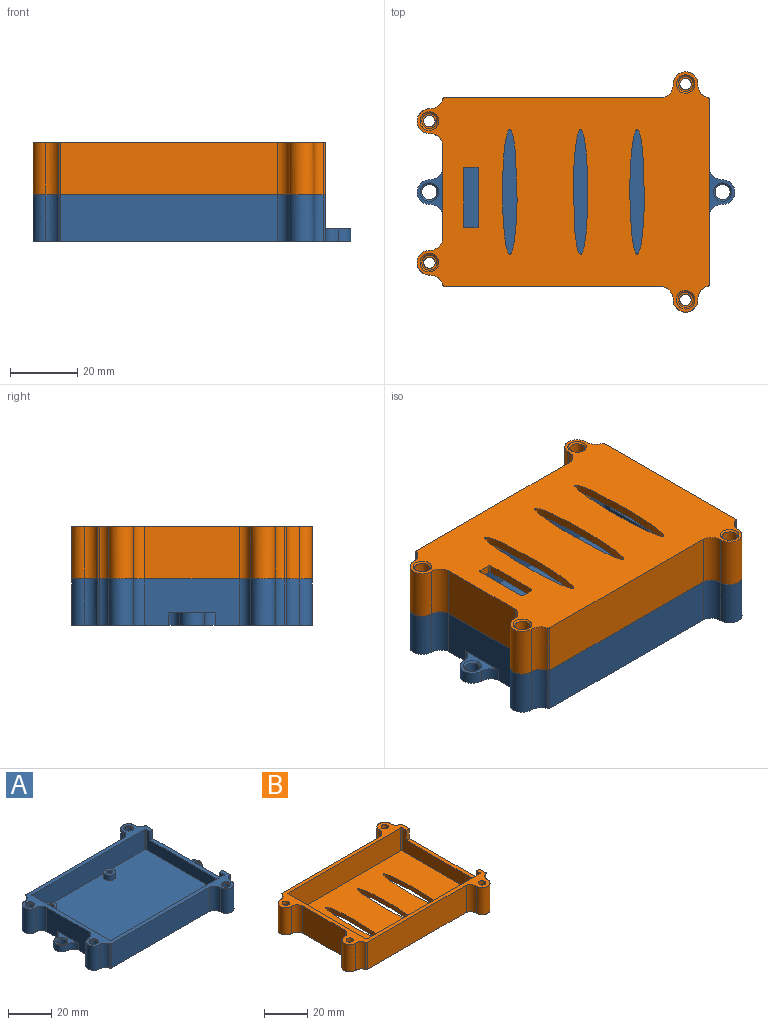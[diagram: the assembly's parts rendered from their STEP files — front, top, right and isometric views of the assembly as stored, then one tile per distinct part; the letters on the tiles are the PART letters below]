
ASSEMBLY  parts=2 mates=1
PART A: 82 faces, bbox 94.3x71.3x13.8 mm
  f0: plane 28x13.8mm, normal (-1,0,0), area 334.6mm2, adj f10,f11,f38,f40,f50,f69,f71
  f1: plane 64.5x13.8mm, normal (0,-1,0), area 890.1mm2, adj f14,f15,f50,f71
  f2: plane 55x13.8mm, normal (1,0,0), area 481.8mm2, adj f18,f19,f28,f29,f41,f43,f50,f68
  f3: plane 51x11.5mm, normal (-1,0,0), area 361.1mm2, adj f25,f26,f28,f29,f51,f68,f71
  f4: cylinder r=3.65mm len=13.8mm, axis (0,0,-1), area 162.5mm2, adj f5,f20,f50,f71
  f5: cylinder r=4mm len=13.8mm, axis (0,0,-1), area 70.8mm2, adj f4,f6,f50,f71
  f6: plane 65x13.8mm, normal (0,1,0), area 897mm2, adj f5,f7,f50,f71
  f7: cylinder r=0.5mm len=13.8mm, axis (0,0,-1), area 10.8mm2, adj f6,f8,f50,f71
  f8: cylinder r=4mm len=13.8mm, axis (0,0,-1), area 70.8mm2, adj f7,f9,f50,f71
  f9: cylinder r=3.65mm len=13.8mm, axis (0,0,-1), area 161.1mm2, adj f8,f10,f50,f71
  f10: cylinder r=4mm len=13.8mm, axis (0,0,-1), area 77.7mm2, adj f0,f9,f50,f71
  f11: cylinder r=4mm len=13.8mm, axis (0,0,-1), area 77.7mm2, adj f0,f12,f50,f71
  f12: cylinder r=3.65mm len=13.8mm, axis (0,0,-1), area 161.1mm2, adj f11,f13,f50,f71
  f13: cylinder r=4mm len=13.8mm, axis (0,0,-1), area 70.8mm2, adj f12,f14,f50,f71
  f14: cylinder r=0.5mm len=13.8mm, axis (0,0,-1), area 10.8mm2, adj f1,f13,f50,f71
  f15: cylinder r=4mm len=13.8mm, axis (0,0,-1), area 77.7mm2, adj f1,f16,f50,f71
  f16: cylinder r=3.65mm len=13.8mm, axis (0,0,-1), area 161.1mm2, adj f15,f17,f50,f71
  f17: cylinder r=4mm len=13.8mm, axis (0,0,-1), area 70.8mm2, adj f16,f18,f50,f71
  f18: cylinder r=0.5mm len=13.8mm, axis (0,0,-1), area 10.8mm2, adj f2,f17,f50,f71
  f19: cylinder r=0.5mm len=13.8mm, axis (0,0,-1), area 10.8mm2, adj f2,f20,f50,f71
  f20: cylinder r=4mm len=13.8mm, axis (0,0,-1), area 70.8mm2, adj f4,f19,f50,f71
  f21: cylinder r=0.5mm len=11.5mm, axis (0,0,-1), area 9mm2, adj f22,f27,f51,f71
  f22: plane 51x11.5mm, normal (1,0,0), area 586.5mm2, adj f21,f23,f51,f71
  f23: cylinder r=0.5mm len=11.5mm, axis (0,0,-1), area 9mm2, adj f22,f24,f51,f71
  f24: plane 74x11.5mm, normal (0,-1,0), area 851mm2, adj f23,f25,f51,f71
  f25: cylinder r=0.5mm len=11.5mm, axis (0,0,-1), area 9mm2, adj f3,f24,f51,f71
  f26: cylinder r=0.5mm len=11.5mm, axis (0,0,-1), area 9mm2, adj f3,f27,f51,f71
  f27: plane 74x11.5mm, normal (0,1,0), area 851mm2, adj f21,f26,f51,f71
  f28: plane 4.9x2mm, normal (0,-1,0), area 9.8mm2, adj f2,f3,f68,f71
  f29: plane 4.9x2mm, normal (0,1,0), area 9.8mm2, adj f2,f3,f68,f71
  f30: cylinder r=2.25mm len=4.5mm, axis (0,0,-1), area 7.1mm2, adj f37,f71
  f31: cylinder r=2.25mm len=4.5mm, axis (0,0,-1), area 7.1mm2, adj f36,f71
  f32: cylinder r=2.25mm len=4.5mm, axis (0,0,-1), area 7.1mm2, adj f35,f71
  f33: cylinder r=2.25mm len=4.5mm, axis (0,0,-1), area 7.1mm2, adj f34,f71
  f34: plane 4.5x4.5mm, normal (0,0,1), area 4.6mm2, adj f33,f77
  f35: plane 4.5x4.5mm, normal (0,0,1), area 4.6mm2, adj f32,f76
  f36: plane 4.5x4.5mm, normal (0,0,1), area 4.6mm2, adj f31,f74
  f37: plane 4.5x4.5mm, normal (0,0,1), area 4.6mm2, adj f30,f75
  f38: cylinder r=4mm len=3.95mm, axis (0,0,-1), area 20.8mm2, adj f0,f39,f50,f69
  f39: cylinder r=3.65mm len=7.3mm, axis (0,0,-1), area 42.8mm2, adj f38,f40,f50,f69
  f40: cylinder r=4mm len=3.95mm, axis (0,0,-1), area 20.8mm2, adj f0,f39,f50,f69
  f41: cylinder r=4mm len=3.95mm, axis (0,0,-1), area 20.8mm2, adj f2,f42,f50,f70
  f42: cylinder r=3.65mm len=7.3mm, axis (0,0,-1), area 42.8mm2, adj f41,f43,f50,f70
  f43: cylinder r=4mm len=3.95mm, axis (0,0,-1), area 20.8mm2, adj f2,f42,f50,f70
  f44: cylinder r=2.25mm len=4.5mm, axis (0,0,-1), area 45.2mm2, adj f50,f72
  f45: cylinder r=1.7mm len=13.1mm, axis (0,0,-1), area 139.9mm2, adj f50,f77
  f46: cylinder r=1.7mm len=13.1mm, axis (0,0,-1), area 139.9mm2, adj f50,f76
  f47: cylinder r=1.7mm len=13.1mm, axis (0,0,-1), area 139.9mm2, adj f50,f74
  f48: cylinder r=1.7mm len=13.1mm, axis (0,0,-1), area 139.9mm2, adj f50,f75
  f49: cylinder r=2.25mm len=4.5mm, axis (0,0,-1), area 45.2mm2, adj f50,f73
  f50: plane 94.3x71.3mm, normal (0,0,-1), area 4693.5mm2, adj f0,f1,f2,f4,f5,f6,f7,f8
  f51: plane 75x52mm, normal (0,0,1), area 3804.8mm2, adj f3,f21,f22,f23,f24,f25,f26,f27
  f52: cylinder r=1.3mm len=2.8mm, axis (0,0,-1), area 22.9mm2, adj f55,f81
  f53: cylinder r=2.75mm len=5.5mm, axis (0,0,-1), area 51.8mm2, adj f51,f54
  f54: plane 5.5x5.5mm, normal (0,0,1), area 16.7mm2, adj f53,f81
  f55: plane 2.6x2.6mm, normal (0,0,1), area 5.3mm2, adj f52
  f56: cylinder r=1.3mm len=2.8mm, axis (0,0,-1), area 22.9mm2, adj f59,f80
  f57: cylinder r=2.75mm len=5.5mm, axis (0,0,-1), area 51.8mm2, adj f51,f58
  f58: plane 5.5x5.5mm, normal (0,0,1), area 16.7mm2, adj f57,f80
  f59: plane 2.6x2.6mm, normal (0,0,1), area 5.3mm2, adj f56
  f60: cylinder r=1.3mm len=2.8mm, axis (0,0,-1), area 22.9mm2, adj f63,f79
  f61: cylinder r=2.75mm len=5.5mm, axis (0,0,-1), area 51.8mm2, adj f51,f62
  f62: plane 5.5x5.5mm, normal (0,0,1), area 16.7mm2, adj f61,f79
  f63: plane 2.6x2.6mm, normal (0,0,1), area 5.3mm2, adj f60
  f64: cylinder r=1.3mm len=2.8mm, axis (0,0,-1), area 22.9mm2, adj f67,f78
  f65: cylinder r=2.75mm len=5.5mm, axis (0,0,-1), area 51.8mm2, adj f51,f66
  f66: plane 5.5x5.5mm, normal (0,0,1), area 16.7mm2, adj f65,f78
  f67: plane 2.6x2.6mm, normal (0,0,1), area 5.3mm2, adj f64
  f68: plane 46x2mm, normal (0,0,1), area 92mm2, adj f2,f3,f28,f29
  f69: plane 14x7.65mm, normal (0,0,1), area 32.9mm2, adj f0,f38,f39,f40,f73
  f70: plane 14x7.65mm, normal (0,0,1), area 32.9mm2, adj f2,f41,f42,f43,f72
  f71: plane 86.65x71.3mm, normal (0,0,1), area 593mm2, adj f0,f1,f2,f3,f4,f5,f6,f7
  f72: cone r=2.25mm half-angle=45deg, axis (0,0,1), area 11.1mm2, adj f44,f70
  f73: cone r=2.25mm half-angle=45deg, axis (0,0,1), area 11.1mm2, adj f49,f69
  f74: cone r=1.7mm half-angle=45deg, axis (0,0,1), area 3.2mm2, adj f36,f47
  f75: cone r=1.7mm half-angle=45deg, axis (0,0,1), area 3.2mm2, adj f37,f48
  f76: cone r=1.7mm half-angle=45deg, axis (0,0,1), area 3.2mm2, adj f35,f46
  f77: cone r=1.7mm half-angle=45deg, axis (0,0,1), area 3.2mm2, adj f34,f45
  f78: cone r=1.3mm half-angle=45deg, axis (0,0,1), area 2.5mm2, adj f64,f66
  f79: cone r=1.3mm half-angle=45deg, axis (0,0,1), area 2.5mm2, adj f60,f62
  f80: cone r=1.3mm half-angle=45deg, axis (0,0,1), area 2.5mm2, adj f56,f58
  f81: cone r=1.3mm half-angle=45deg, axis (0,0,1), area 2.5mm2, adj f52,f54
PART B: 61 faces, bbox 86.7x71.3x15.5 mm
  f0: cone r=2.25mm half-angle=45deg, axis (0,0,-1), area 11.1mm2, adj f15,f51
  f1: cone r=2.25mm half-angle=45deg, axis (0,0,-1), area 11.1mm2, adj f15,f57
  f2: cone r=2.25mm half-angle=45deg, axis (0,0,-1), area 11.1mm2, adj f15,f48
  f3: cone r=2.25mm half-angle=45deg, axis (0,0,-1), area 11.1mm2, adj f15,f54
  f4: extruded ~37x4.4mm, area 189.5mm2, adj f15,f16
  f5: extruded ~37x4.4mm, area 189.5mm2, adj f15,f16
  f6: extruded ~37x4.4mm, area 189.5mm2, adj f15,f16
  f7: plane 3.5x2.5mm, normal (0,1,0), area 8.7mm2, adj f8,f14,f15,f16
  f8: cylinder r=0.5mm len=2.5mm, axis (0,0,1), area 2mm2, adj f7,f9,f15,f16
  f9: plane 17x2.5mm, normal (-1,0,0), area 42.5mm2, adj f8,f10,f15,f16
  f10: cylinder r=0.5mm len=2.5mm, axis (0,0,1), area 2mm2, adj f9,f11,f15,f16
  f11: plane 3.5x2.5mm, normal (0,-1,0), area 8.7mm2, adj f10,f12,f15,f16
  f12: cylinder r=0.5mm len=2.5mm, axis (0,0,1), area 2mm2, adj f11,f13,f15,f16
  f13: plane 17x2.5mm, normal (1,0,0), area 42.5mm2, adj f12,f14,f15,f16
  f14: cylinder r=0.5mm len=2.5mm, axis (0,0,1), area 2mm2, adj f7,f13,f15,f16
  f15: plane 86.65x71.3mm, normal (0,0,-1), area 4089mm2, adj f0,f1,f2,f3,f4,f5,f6,f7
  f16: plane 75x52mm, normal (0,0,1), area 3435.4mm2, adj f4,f5,f6,f7,f8,f9,f10,f11
  f17: plane 46x2mm, normal (0,0,1), area 92mm2, adj f18,f19,f27,f36
  f18: plane 5.6x2mm, normal (0,-1,0), area 11.2mm2, adj f17,f27,f36,f60
  f19: plane 5.6x2mm, normal (0,1,0), area 11.2mm2, adj f17,f27,f36,f60
  f20: plane 74x13mm, normal (0,-1,0), area 962mm2, adj f16,f21,f26,f60
  f21: cylinder r=0.5mm len=13mm, axis (0,0,1), area 10.2mm2, adj f16,f20,f27,f60
  f22: cylinder r=0.5mm len=13mm, axis (0,0,1), area 10.2mm2, adj f16,f23,f27,f60
  f23: plane 74x13mm, normal (0,1,0), area 962mm2, adj f16,f22,f24,f60
  f24: cylinder r=0.5mm len=13mm, axis (0,0,1), area 10.2mm2, adj f16,f23,f25,f60
  f25: plane 51x13mm, normal (1,0,0), area 663mm2, adj f16,f24,f26,f60
  f26: cylinder r=0.5mm len=13mm, axis (0,0,1), area 10.2mm2, adj f16,f20,f25,f60
  f27: plane 51x13mm, normal (-1,0,0), area 405.4mm2, adj f16,f17,f18,f19,f21,f22,f60
  f28: cylinder r=0.5mm len=15.5mm, axis (0,0,1), area 12.2mm2, adj f15,f29,f36,f60
  f29: cylinder r=4mm len=15.5mm, axis (0,0,1), area 81.6mm2, adj f15,f28,f30,f60
  f30: cylinder r=3.65mm len=15.5mm, axis (0,0,1), area 178.8mm2, adj f15,f29,f31,f60
  f31: cylinder r=4mm len=15.5mm, axis (0,0,1), area 87.3mm2, adj f15,f30,f46,f60
  f32: cylinder r=4mm len=15.5mm, axis (0,0,1), area 81.6mm2, adj f15,f35,f41,f60
  f33: cylinder r=4mm len=15.5mm, axis (0,0,1), area 81.6mm2, adj f15,f34,f35,f60
  f34: cylinder r=0.5mm len=15.5mm, axis (0,0,1), area 12.2mm2, adj f15,f33,f36,f60
  f35: cylinder r=3.65mm len=15.5mm, axis (0,0,1), area 178.4mm2, adj f15,f32,f33,f60
  f36: plane 55x15.5mm, normal (1,0,0), area 594.9mm2, adj f15,f17,f18,f19,f28,f34,f60
  f37: cylinder r=4mm len=15.5mm, axis (0,0,1), area 87.3mm2, adj f15,f38,f47,f60
  f38: cylinder r=3.65mm len=15.5mm, axis (0,0,1), area 178.8mm2, adj f15,f37,f39,f60
  f39: cylinder r=4mm len=15.5mm, axis (0,0,1), area 81.6mm2, adj f15,f38,f40,f60
  f40: cylinder r=0.5mm len=15.5mm, axis (0,0,1), area 12.2mm2, adj f15,f39,f41,f60
  f41: plane 65x15.5mm, normal (0,-1,0), area 1007.5mm2, adj f15,f32,f40,f60
  f42: cylinder r=0.5mm len=15.5mm, axis (0,0,1), area 12.2mm2, adj f15,f43,f46,f60
  f43: cylinder r=4mm len=15.5mm, axis (0,0,1), area 81.6mm2, adj f15,f42,f44,f60
  f44: cylinder r=3.65mm len=15.5mm, axis (0,0,1), area 178.8mm2, adj f15,f43,f45,f60
  f45: cylinder r=4mm len=15.5mm, axis (0,0,1), area 87.3mm2, adj f15,f44,f47,f60
  f46: plane 64.5x15.5mm, normal (0,1,0), area 999.7mm2, adj f15,f31,f42,f60
  f47: plane 28x15.5mm, normal (-1,0,0), area 434mm2, adj f15,f37,f45,f60
  f48: cylinder r=2.25mm len=13mm, axis (0,0,1), area 183.8mm2, adj f2,f49
  f49: plane 4.5x4.5mm, normal (0,0,-1), area 6.8mm2, adj f48,f50
  f50: cylinder r=1.7mm len=3.4mm, axis (0,0,1), area 21.4mm2, adj f49,f60
  f51: cylinder r=2.25mm len=13mm, axis (0,0,1), area 183.8mm2, adj f0,f52
  f52: plane 4.5x4.5mm, normal (0,0,-1), area 6.8mm2, adj f51,f53
  f53: cylinder r=1.7mm len=3.4mm, axis (0,0,1), area 21.4mm2, adj f52,f60
  f54: cylinder r=2.25mm len=13mm, axis (0,0,1), area 183.8mm2, adj f3,f55
  f55: plane 4.5x4.5mm, normal (0,0,-1), area 6.8mm2, adj f54,f56
  f56: cylinder r=1.7mm len=3.4mm, axis (0,0,1), area 21.4mm2, adj f55,f60
  f57: cylinder r=2.25mm len=13mm, axis (0,0,1), area 183.8mm2, adj f1,f58
  f58: plane 4.5x4.5mm, normal (0,0,-1), area 6.8mm2, adj f57,f59
  f59: cylinder r=1.7mm len=3.4mm, axis (0,0,1), area 21.4mm2, adj f58,f60
  f60: plane 86.65x71.3mm, normal (0,0,1), area 620.3mm2, adj f18,f19,f20,f21,f22,f23,f24,f25
PLACE A t=(83.05,-43.63,2.86)mm
PLACE B rot(axis=(-1,0,0),180deg) t=(83.05,-43.63,32.01)mm
MATE cylindrical A.f9 <-> B.f54  axis (0,0,-1) through (39.55,-22.63,9.41)mm
